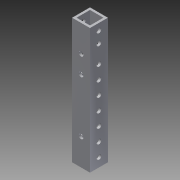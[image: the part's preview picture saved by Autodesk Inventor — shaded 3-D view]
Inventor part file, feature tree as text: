
AUTODESK INVENTOR PART (.ipt)
format: ipt  version: 2013 (Build 170138000, 138)  size: 146,432 bytes
history: native  units: in
note: dims shown in document units (in); Inventor stores cm internally (conversion verified against a paired STEP export)
features: extrude x4, sketch x4, reference x2
ambient origin geometry x8: Origin, YZ Plane, XZ Plane, XY Plane, X Axis, Y Axis, Z Axis, Center Point
bodies: Solid1 (feature_tree)
feature tree (10):
  extrude  "Extrusion1"  Depth=1.0in
  extrude  "Extrusion2"  Depth=7.0in TaperAngle=0.0deg
  extrude  "Extrusion3"  Depth=0.26in
  extrude  "Extrusion4"  Depth=4.25in
  sketch  "Sketch1"  dims[d0=1.0in d1=1.0in]
  sketch  "Sketch2"  dims[d2=0.125in d3=7.0in d4=0.0in]
  reference  "Reference5"
  reference  "Reference6"
  sketch  "Sketch3"  dims[d6=1.0in d7=0.0in d16=0.26in]
  sketch  "Sketch4"  dims[d17=0.26in d18=4.25in d19=0.26in d20=0.5in d21=0.5in d22=0.26in d23=1.0in d24=2.3622in d26=0.75in d27=0.3937in d29=1.0in d31=1.0in d32=0.0in d33=0.26in d35=1.5in d36=1.9685in d38=1.0in d39=0.3937in d41=1.0in d43=1.0in d44=0.0in]
